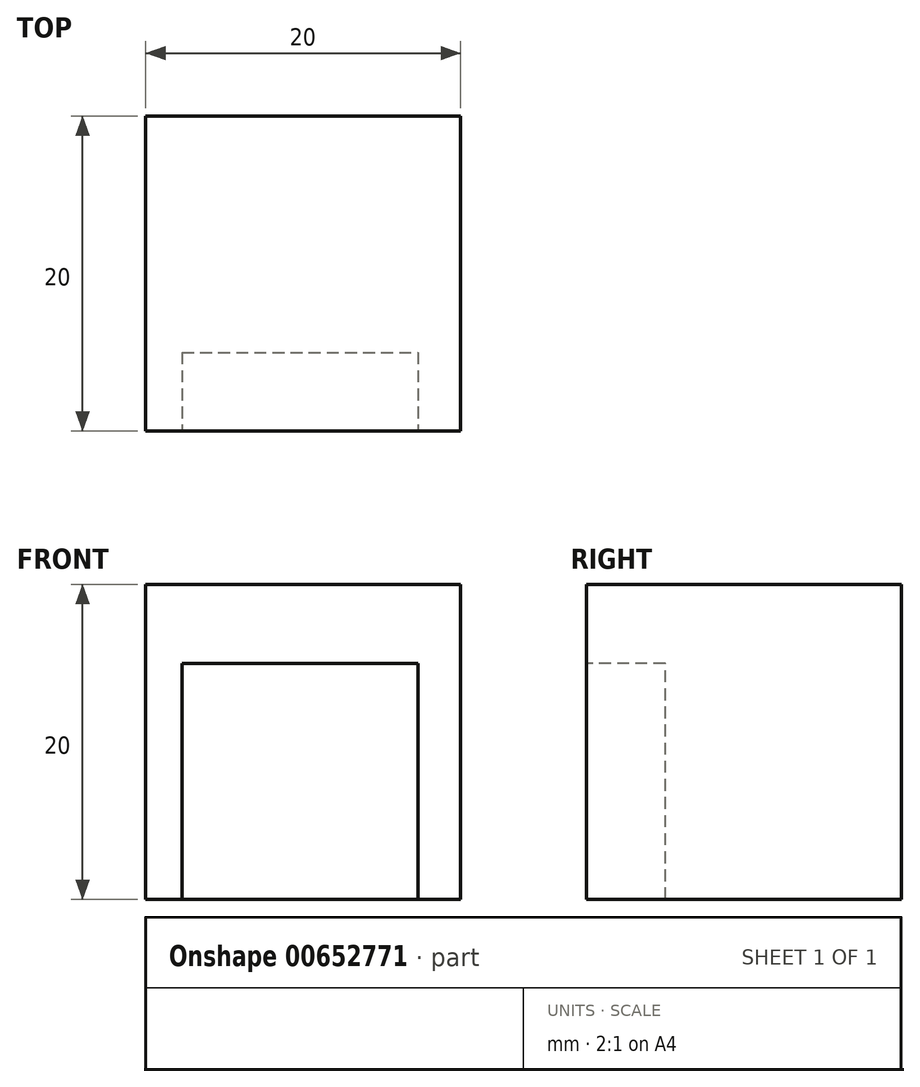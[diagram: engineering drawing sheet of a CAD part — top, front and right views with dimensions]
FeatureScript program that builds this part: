
annotation { "Feature Type Name" : "Feature", "Feature Type Description" : "" }
export const myFeature = defineFeature(function(context is Context, id is Id, definition is map)
    precondition{}
    {
        {
            var Q0;
            Q0=qCreatedBy(makeId("Top.planeOp"),FACE);
            var sketch = newSketch(context, id + "F0", { "sketchPlane" : qUnion([Q0])});
            skLineSegment(sketch, "E0.bottom", {"start": v(0, 0) * mm, "end": v(20, 0) * mm});
            skLineSegment(sketch, "E0.top", {"start": v(0, -20) * mm, "end": v(20, -20) * mm});
            skLineSegment(sketch, "E0.left", {"start": v(0, 0) * mm, "end": v(0, -20) * mm});
            skLineSegment(sketch, "E0.right", {"start": v(20, 0) * mm, "end": v(20, -20) * mm});
            skSolve(sketch);
        }
        {
            var Q0;
            Q0 = qSketchRegion(id + "F0", true);
            extrude(context, id + "F1", {"entities" : qUnion([Q0]), "depth" : 20 * mm, "offsetDistance" : 25 * mm});
        }
        {
            var Q0;
            Q0=makeQuery(id+"F1.opExtrude","SWEPT_FACE",FACE,{"disambiguationData":[OSD([sQuery(id+"F0.wireOp",EDGE,"E0.top")])]});
            var sketch = newSketch(context, id + "F2", { "sketchPlane" : qUnion([Q0])});
            skLineSegment(sketch, "E1.bottom", {"start": v(17.3, 0) * mm, "end": v(2.3, 0) * mm});
            skLineSegment(sketch, "E1.top", {"start": v(17.3, 15) * mm, "end": v(2.3, 15) * mm});
            skLineSegment(sketch, "E1.left", {"start": v(17.3, 0) * mm, "end": v(17.3, 15) * mm});
            skLineSegment(sketch, "E1.right", {"start": v(2.3, 0) * mm, "end": v(2.3, 15) * mm});
            skPoint(sketch, "E1.middle", {"position": v(9.8, 7.5) * mm});
            skSolve(sketch);
        }
        {
            var Q0;
            Q0=makeQuery(id+"F2.imprint","IMPRINT",FACE,{"disambiguationData":[TD([[makeQuery(id+"F2.imprint","IMPRINT",EDGE,{"derivedFrom":sQuery(id+"F2.wireOp",EDGE,"E1.bottom")}),1.0]])]});
            extrude(context, id + "F3", {"entities" : qUnion([Q0]), "operationType" : NewBodyOperationType.REMOVE, "oppositeDirection" : true, "depth" : 5 * mm, "offsetDistance" : 25 * mm});
        }
    });
